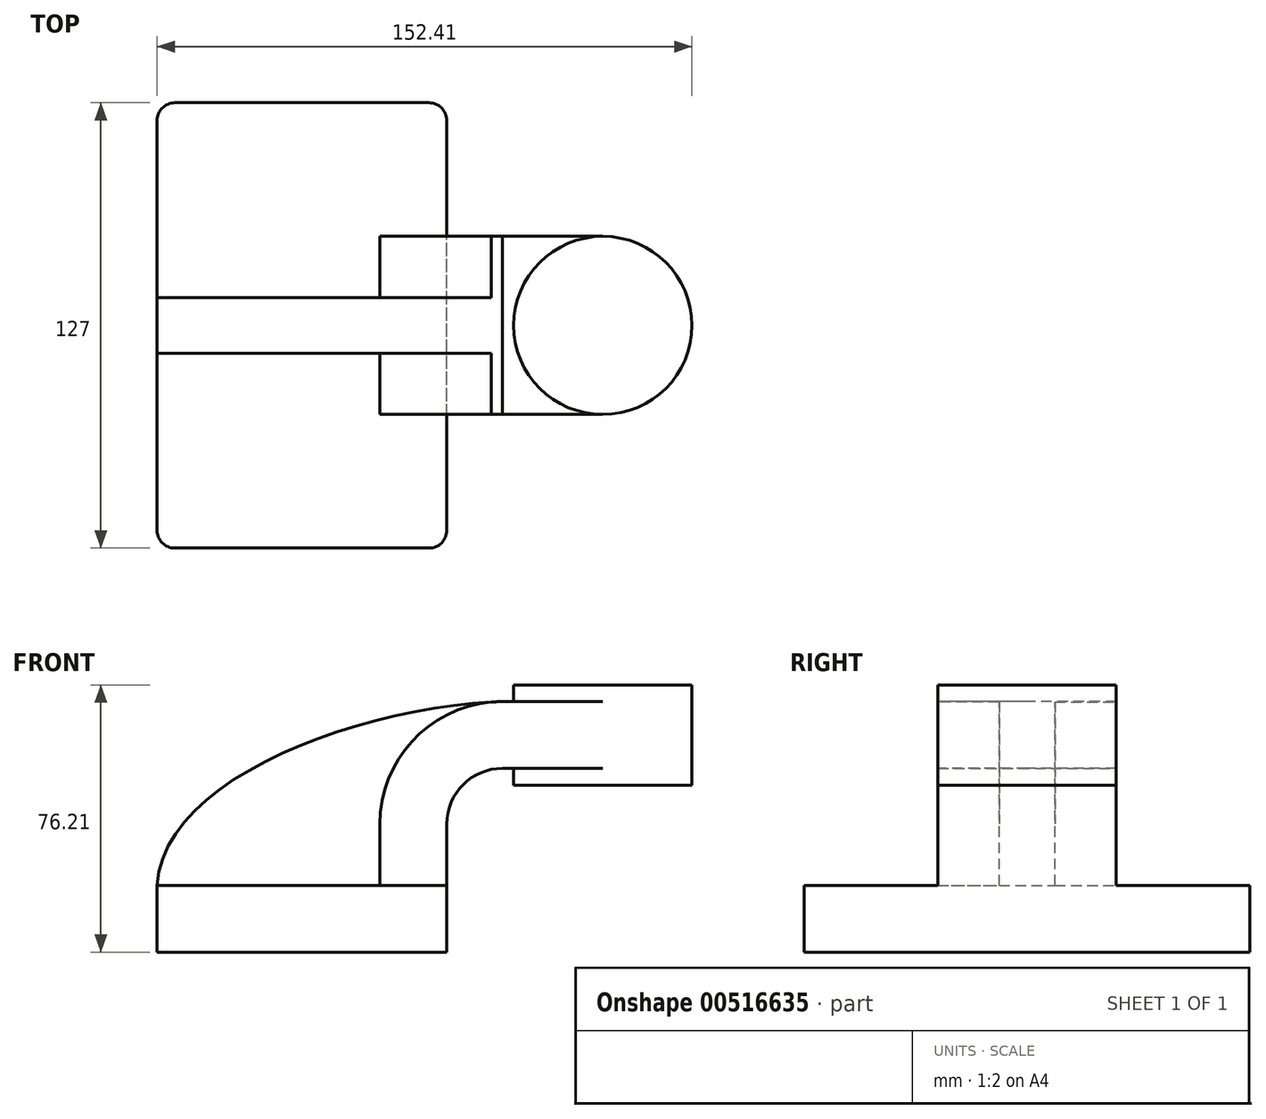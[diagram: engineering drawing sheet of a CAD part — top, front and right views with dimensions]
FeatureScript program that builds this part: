
annotation { "Feature Type Name" : "Feature", "Feature Type Description" : "" }
export const myFeature = defineFeature(function(context is Context, id is Id, definition is map)
    precondition{}
    {
        {
            var Q0;
            Q0=qCreatedBy(makeId("Front.planeOp"),FACE);
            var sketch = newSketch(context, id + "F0", { "sketchPlane" : qUnion([Q0])});
            skLineSegment(sketch, "E0.rect.bottom", {"start": v(-41.28, 9.52) * mm, "end": v(41.28, 9.52) * mm});
            skLineSegment(sketch, "E0.rect.top", {"start": v(-41.28, -9.52) * mm, "end": v(41.28, -9.52) * mm});
            skLineSegment(sketch, "E0.rect.left", {"start": v(-41.28, 9.52) * mm, "end": v(-41.28, -9.52) * mm});
            skLineSegment(sketch, "E0.rect.right", {"start": v(41.28, 9.52) * mm, "end": v(41.28, -9.52) * mm});
            skPoint(sketch, "E0.rect.middle", {"position": v(0, 0) * mm});
            skLineSegment(sketch, "E1", {"start": v(41.28, 9.52) * mm, "end": v(41.28, 27) * mm});
            skArc(sketch, "E2", {"start": v(41.28, 27) * mm, "mid": v(45.92, 38.23) * mm, "end": v(57.15, 42.88) * mm});
            skLineSegment(sketch, "E3", {"start": v(57.15, 42.88) * mm, "end": v(85.72, 42.88) * mm});
            skLineSegment(sketch, "E4.rect.bottom", {"start": v(60.32, 38.1) * mm, "end": v(111.12, 38.1) * mm});
            skLineSegment(sketch, "E4.rect.top", {"start": v(60.32, 66.68) * mm, "end": v(111.12, 66.68) * mm});
            skLineSegment(sketch, "E4.rect.left", {"start": v(60.32, 38.1) * mm, "end": v(60.32, 66.68) * mm});
            skLineSegment(sketch, "E4.rect.right", {"start": v(111.13, 38.1) * mm, "end": v(111.12, 66.68) * mm});
            skPoint(sketch, "E4.rect.middle", {"position": v(85.72, 52.39) * mm});
            skLineSegment(sketch, "E5.0", {"start": v(57.15, 61.93) * mm, "end": v(85.72, 61.93) * mm});
            skArc(sketch, "E5.1", {"start": v(22.23, 27) * mm, "mid": v(32.45, 51.7) * mm, "end": v(57.15, 61.93) * mm});
            skLineSegment(sketch, "E5.2", {"start": v(22.23, 9.52) * mm, "end": v(22.23, 27) * mm});
            skLineSegment(sketch, "E6", {"start": v(85.72, 38.1) * mm, "end": v(85.72, 66.68) * mm});
            skFitSpline(sketch, "E7", {"points": [v(-41.28, 9.53) * mm, v(57.15, 61.93) * mm], "startDerivative": vector(5.2, 92.34) * mm, "endDerivative": vector(120.92, 4.22) * mm});
            skSolve(sketch);
        }
        {
            var Q0;
            Q0=makeQuery(id+"F0.imprint","IMPRINT",FACE,{"disambiguationData":[TD([[makeQuery(id+"F0.imprint","IMPRINT",EDGE,{"derivedFrom":sQuery(id+"F0.wireOp",EDGE,"E0.rect.top")}),1.0]])]});
            extrude(context, id + "F1", {"entities" : qUnion([Q0]), "endBound" : BoundingType.SYMMETRIC, "depth" : 127 * mm});
        }
        {
            var Q0;
            {var subQ9=sQuery(id+"F0.wireOp",EDGE,"E1");Q0=makeQuery(id+"F0.imprint","IMPRINT",FACE,{"disambiguationData":[TD([[makeQuery(id+"F0.imprint","IMPRINT",EDGE,{"derivedFrom":subQ9}),1.0]])]});}
            var Q1;
            {var subQ0=sQuery(id+"F0.wireOp",EDGE,"E6");var subQ1=sQuery(id+"F0.wireOp",EDGE,"E3");var subQ2=makeQuery(id+"F0.imprint","INTERSECT",VERTEX,{"derivedFrom":[subQ1,subQ0]});Q1=makeQuery(id+"F0.imprint","IMPRINT",FACE,{"disambiguationData":[TD([[makeQuery(id+"F0.imprint","IMPRINT",EDGE,{"disambiguationData":[TD([[subQ2,1.0]])],"derivedFrom":subQ1}),1.0]])]});}
            extrude(context, id + "F2", {"entities" : qUnion([Q0, Q1]), "operationType" : NewBodyOperationType.ADD, "endBound" : BoundingType.SYMMETRIC, "depth" : 50.8 * mm});
        }
        {
            var Q0;
            {var subQ3=sQuery(id+"F0.wireOp",EDGE,"E5.2");Q0=makeQuery(id+"F0.imprint","IMPRINT",FACE,{"disambiguationData":[TD([[makeQuery(id+"F0.imprint","IMPRINT",EDGE,{"derivedFrom":subQ3}),1.0]])]});}
            extrude(context, id + "F3", {"entities" : qUnion([Q0]), "operationType" : NewBodyOperationType.ADD, "endBound" : BoundingType.SYMMETRIC, "depth" : 15.88 * mm});
        }
        {
            var Q0;
            {var subQ0=sQuery(id+"F0.wireOp",EDGE,"E4.rect.right");Q0=makeQuery(id+"F0.imprint","IMPRINT",FACE,{"disambiguationData":[TD([[makeQuery(id+"F0.imprint","IMPRINT",EDGE,{"derivedFrom":subQ0}),1.0]])]});}
            var Q1;
            Q1=sQuery(id+"F0.wireOp",EDGE,"E6");
            revolve(context, id + "F4", {"entities" : qUnion([Q0]), "axis" : qUnion([Q1]), "revolveType" : RevolveType.FULL});
        }
        {
            var Q0;
            {var subQ5=sQuery(id+"F0.wireOp",EDGE,"E4.rect.right");Q0=makeQuery(id+"F0.imprint","IMPRINT",FACE,{"disambiguationData":[TD([[makeQuery(id+"F0.imprint","IMPRINT",EDGE,{"derivedFrom":subQ5}),1.0]])]});}
            var Q1;
            Q1=sQuery(id+"F0.wireOp",EDGE,"E6");
            revolve(context, id + "F5", {"operationType" : NewBodyOperationType.ADD, "entities" : qUnion([Q0]), "axis" : qUnion([Q1]), "revolveType" : RevolveType.FULL});
        }
        {
            var Q0;
            Q0=makeQuery(id+"F1.opExtrude","CAP_EDGE",EDGE,{"disambiguationData":[OSD([sQuery(id+"F0.wireOp",EDGE,"E0.rect.right")])],"isStart":false});
            var Q1;
            Q1=makeQuery(id+"F1.opExtrude","CAP_EDGE",EDGE,{"disambiguationData":[OSD([sQuery(id+"F0.wireOp",EDGE,"E0.rect.left")])],"isStart":false});
            var Q2;
            Q2=makeQuery(id+"F1.opExtrude","CAP_EDGE",EDGE,{"disambiguationData":[OSD([sQuery(id+"F0.wireOp",EDGE,"E0.rect.right")])],"isStart":true});
            var Q3;
            Q3=makeQuery(id+"F1.opExtrude","CAP_EDGE",EDGE,{"disambiguationData":[OSD([sQuery(id+"F0.wireOp",EDGE,"E0.rect.left")])],"isStart":true});
            fillet(context, id + "F6", {"entities" : qUnion([Q0, Q1, Q2, Q3]), "radius" : 5.08 * mm, "tangentPropagation" : true, "allowEdgeOverflow" : false});
        }
    });
